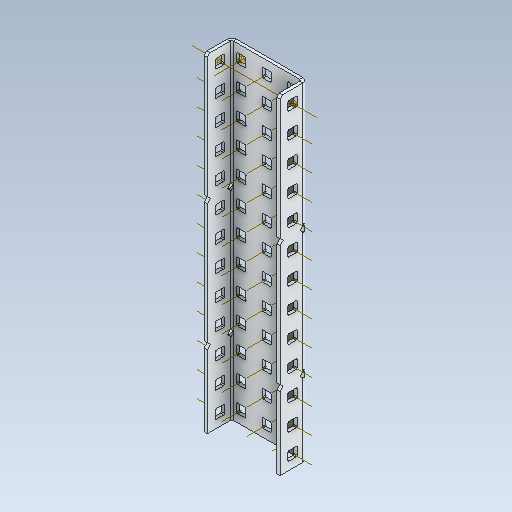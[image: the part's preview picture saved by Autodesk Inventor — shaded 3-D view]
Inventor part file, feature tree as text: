
AUTODESK INVENTOR PART (.ipt)
format: ipt  version: 2020 (Build 240168000, 168)  size: 1,165,824 bytes
history: native  units: in
note: dims shown in document units (in); Inventor stores cm internally (conversion verified against a paired STEP export)
features: other x68, plane x5, pattern_linear x3, split x1, sheet_metal_op x1
ambient origin geometry x8: Origin, YZ Plane, XZ Plane, XY Plane, X Axis, Y Axis, Z Axis, Center Point
bodies: Solid1 (feature_tree)
feature tree (78):
  plane  "Work Plane2"
  plane  "Work Plane1"
  other  "Work Point1"
  other  "Work Point2"
  other  "Work Axis1"
  other  "Work Axis2"
  other  "Work Axis3"
  pattern_linear  "Rectangular Pattern1"  Count1=13 Spacing1=0.5in
  pattern_linear  "Rectangular Pattern2"  Count1=13 Spacing1=0.5in
  pattern_linear  "Rectangular Pattern3"  Count1=13 Spacing1=0.5in
  plane  "Work Plane5"
  split  "Split1"
  plane  "Work Plane3"
  plane  "Work Plane4"
  other  "Work Point3"
  other  "Work Axis4"
  other  "Work Axis5"
  other  "Work Axis6"
  other  "Work Axis7"
  other  "Work Axis8"
  other  "Work Axis9"
  other  "Work Axis10"
  other  "Work Axis11"
  other  "Work Axis12"
  other  "Work Axis13"
  other  "Work Axis14"
  other  "Work Axis15"
  other  "Work Axis38"
  other  "Work Axis39"
  other  "Work Axis40"
  other  "Work Axis41"
  other  "Work Axis42"
  other  "Work Axis43"
  other  "Work Axis44"
  other  "Work Axis45"
  other  "Work Axis46"
  other  "Work Axis47"
  other  "Work Axis48"
  other  "Work Axis49"
  other  "Work Axis72"
  other  "Work Axis73"
  other  "Work Axis74"
  other  "Work Axis75"
  other  "Work Axis76"
  other  "Work Axis77"
  other  "Work Axis78"
  other  "Work Axis79"
  other  "Work Axis80"
  other  "Work Axis81"
  other  "Work Axis82"
  other  "Work Axis83"
  other  "Work Axis106"
  other  "Work Axis107"
  other  "Work Axis108"
  other  "Work Axis109"
  other  "Work Axis110"
  other  "Work Axis111"
  other  "Work Axis112"
  other  "Work Axis113"
  other  "Work Axis114"
  other  "Work Axis115"
  other  "Work Axis116"
  other  "Work Axis117"
  other  "Work Axis118"
  other  "Work Axis141"
  other  "Work Axis142"
  other  "Work Axis143"
  other  "Work Axis144"
  other  "Work Axis145"
  other  "Work Axis146"
  other  "Work Axis147"
  other  "Work Axis148"
  other  "Work Axis149"
  other  "Work Axis150"
  other  "Work Axis151"
  other  "Work Axis152"
  other  "Work Axis153"
  sheet_metal_op  "Fold1"
